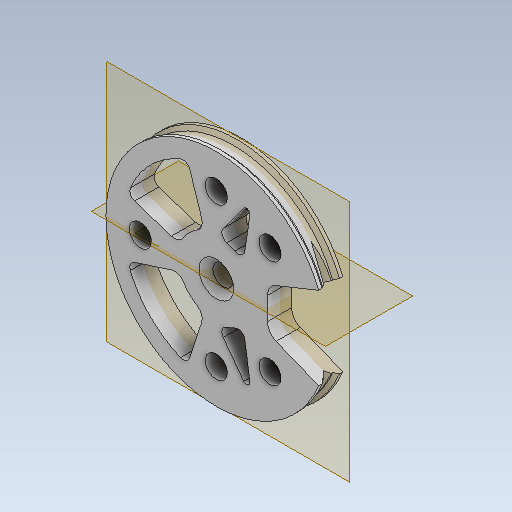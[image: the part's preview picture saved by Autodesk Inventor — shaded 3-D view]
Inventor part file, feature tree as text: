
AUTODESK INVENTOR PART (.ipt)
format: ipt  version: 2020 (Build 240168000, 168)  size: 459,264 bytes
history: native  units: mm
features: sketch x17, extrude x15, projected_geometry x14, other x7, fillet x5, plane x4, reference x4, revolve x2, chamfer x1, mirror x1
ambient origin geometry x8: Origin, YZ Plane, XZ Plane, XY Plane, X Axis, Y Axis, Z Axis, Center Point
bodies: Solid1 (feature_tree)
feature tree (70):
  extrude  "Extrusion1"  Depth=3.5mm TaperAngle=0.0deg
  sketch  "Sketch2"  dims[d3=8.0mm d4=3.5mm d5=0.0mm]
  plane  "Work Plane1"
  extrude  "Extrusion2"  Depth=3.5mm TaperAngle=0.0deg
  extrude  "Extrusion3"  Depth=20.0mm TaperAngle=0.0deg
  plane  "Work Plane2"
  extrude  "Extrusion4"  Depth=10.0mm
  plane  "Work Plane3"
  revolve  "Revolution1"  [1 undecoded]
  extrude  "Extrusion5"  Depth=0.5mm
  extrude  "Extrusion6"  Depth=0.5mm
  fillet  "Fillet1"  Radius=20.0mm
  extrude  "Extrusion7"  TaperAngle=45.0deg  [1 undecoded]
  extrude  "Extrusion8"  Depth=11.0mm
  extrude  "Extrusion9"  Depth=11.0mm
  extrude  "Extrusion10"  Depth=20.0mm TaperAngle=0.0deg
  extrude  "Extrusion11"  Depth=3.839724mm
  extrude  "Extrusion12"  Depth=2.0mm
  fillet  "Fillet2"  Radius=0.7mm
  chamfer  "Chamfer1"  Distance=20.0mm
  extrude  "Extrusion13"  Depth=20.0mm TaperAngle=0.0deg
  fillet  "Fillet3"  Radius=11.0mm
  fillet  "Fillet4"  Radius=3.2mm
  plane  "Work Plane4"
  mirror  "Mirror1"
  fillet  "Fillet5"  Radius=11.0mm
  revolve  "Revolution2"  [1 undecoded]
  extrude  "Extrusion14"  Depth=11.0mm
  extrude  "Extrusion15"  Depth=10.0mm TaperAngle=0.0deg
  sketch  "Sketch1"  dims[d0=32.0mm d1=3.5mm d2=0.0mm]
  reference  "Reference1"
  reference  "Reference2"
  reference  "Reference3"
  reference  "Reference4"
  sketch  "Sketch3"  dims[d6=3.0mm d7=20.0mm d8=0.0mm]
  projected_geometry  "Projected Loop1"
  sketch  "Sketch4"  dims[d9=10.0mm d10=3.0mm]
  projected_geometry  "Projected Loop2"
  sketch  "Sketch5"  dims[d11=3.0mm d12=20.0mm d13=0.0mm]
  projected_geometry  "Projected Loop3"
  projected_geometry  "Projected Loop4"
  sketch  "Sketch6"  dims[d14=1.5mm d15=0.5mm]
  projected_geometry  "Projected Loop5"
  sketch  "Sketch7"  dims[d16=0.5mm d17=0.5mm d18=20.0mm]
  projected_geometry  "Projected Loop6"
  sketch  "Sketch8"  dims[d19=90.0deg d20=45.0deg]
  projected_geometry  "Projected Loop7"
  sketch  "Sketch9"  dims[d21=45.0deg d22=11.0mm]
  projected_geometry  "Projected Loop8"
  sketch  "Sketch10"  dims[d23=3.2mm d24=11.0mm]
  sketch  "Sketch11"  dims[d25=3.2mm d26=20.0mm d27=0.0mm]
  projected_geometry  "Projected Loop9"
  sketch  "Sketch12"  dims[d28=3.839724mm d29=3.839724mm]
  projected_geometry  "Projected Loop10"
  sketch  "Sketch13"  dims[d30=20.0mm d31=0.0mm d32=2.0mm d33=0.7mm d34=20.0mm d35=0.0mm]
  projected_geometry  "Projected Loop11"
  sketch  "Sketch14"  dims[d36=0.7mm d37=20.0mm d38=0.0mm d41=11.0mm d42=3.2mm d43=11.0mm]
  projected_geometry  "Projected Loop12"
  sketch  "Sketch15"  dims[d44=3.2mm d45=20.0mm d46=0.0mm]
  sketch  "Sketch16"  dims[d47=20.0mm d48=0.0mm d49=11.0mm]
  projected_geometry  "Projected Loop13"
  sketch  "Sketch17"  dims[d50=3.2mm d51=20.0mm d52=0.0mm d53=27.0mm d54=11.0mm d55=3.141593mm d56=3.141593mm d57=3.141593mm d58=3.141593mm d59=20.0mm d60=0.0mm d61=1.5mm d62=1.0mm d63=1.0mm d64=2.0mm d65=45.0deg d66=11.0mm d67=13.5mm d68=20.0mm d69=0.0mm d70=0.5mm d71=1.0mm d72=1.5mm d76=0.5mm d77=0.5mm d78=5.0mm d79=360.0deg d80=10.0mm d81=0.0mm d82=10.0mm d83=0.0mm]
  projected_geometry  "Projected Loop14"
  parser-record x1  (decoder bookkeeping rows leaked as tree rows — omitted from the tree; the rows remain in map.json)
  other  "reducer_1.iam"
  other  "bearing_3_6_2:1"
  other  "tendon_wh_1:1"
  other  "mot_holder_1:1"
  other  "mot_27_ass:1"
  other  "mot_27_1:1"
note: 3 required parameter values undecoded (feature->parameter linkage not recoverable at this tier; creation-order binding heuristic only, values carry confidence <= 0.55)
note: 1 file-system path scrubbed to <path> (originals preserved in map.json)